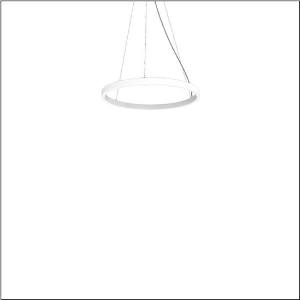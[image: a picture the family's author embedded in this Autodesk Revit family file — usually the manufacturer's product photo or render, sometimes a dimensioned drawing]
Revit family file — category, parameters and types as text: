
# Revit family: silica_r__21_ring-o_5pjbo1d1004a_fa3a
name_source: partatom
category: Lighting Fixtures
units: mm (PartAtom-declared; Revit-internal decimal feet)

## family parameters
Cut with Voids When Loaded = No
Host = Face
Light Source = No
Part Type = Normal
Room Calculation Point = No
Round Connector Dimension = Use Diameter
Shared = No

## types (1)
- Silica® 21 Ring-O (1 x LED, 3740 lm, 60 W, 3000K)
    Apparent Load = 60 VA
    CIE Flux Codes = 2 16 49 50 100
    Color Rendering = 80
    Color Temperature = 3000K
    Default Elevation = 1800 mm
    Description = Silica® 21 Ring-O, suspended luminaire, of PMMA, frosted, light emission: outer ring side luminous distribution, primary light characteristic: symmetric, installation type: suspended mounting, LED, rated luminous flux: 3.744lm, luminous efficacy: 62lm/W, light colour: 830, colour temperature: 3000K, with terminal, 5-pole, mains connection: 230V, AC/DC, 0/50..60Hz, rated input power: 60W, housing, of extruded aluminium section, traffic white (RAL 9016), diameter: 610mm, ceiling canopy, traffic white (RAL 9016), protection rating (lamp compartment): IP40, insulation class (complete): insulation class I (protective earthing), certification: CE, impact resistance: IK02, permissible operating ambient temperature: 0..+35°C, packaging unit: 1 piece
    Height = 48 mm  [stored 0.15748 ft]
    Lamp = 1 x LED
    Lamp Light Flux = 3740 lm
    Lamp Power = 60 W
    Lamp count = 1
    Length = 610 mm
    Luminous efficacy = 62 lm/W
    Manufacturer = Siteco
    ModVariant = No
    Model = 5PJBO1D1004A
    Mounting Place = Ceiling
    Mounting Type = Pendant
    Number of Poles = 1
    OnlyDefault = Yes
    Power Factor = 1
    Product Name = Silica® 21 Ring-O
    Product group = suspended luminaire
    ProductGroupID = 904
    Protection Class = Protection class I
    Protection Degree = Degree of protection
    RLX_Detail_Level = 1
    RLX_Emergency_Light_Flux = 0 lm
    RLX_Emergency_Type = 0
    RLX_Emergency_Type_DB = No
    RlxData = <blob elided: 10577 chars, md5=a55d9a08>
    Socket = socket
    Standby Power = 0 W
    System Light Flux = 3740 lm
    System Power = 60 W
    Type Comments = Product without accessories
    Type Image = l_1258379.jpg
    URL = http://relux.com
    VarID = ---
    Voltage = 0 V
    Weight = 0.00 kg
    Width = 0 mm  [stored 0 ft]

note: [stored X ft] marks values corroborated as IEEE doubles in the binary element streams (Revit-internal decimal feet)

## geometry (parser evidence)
native form markers: Sweep x12
no freeform markers — native parametric forms only
